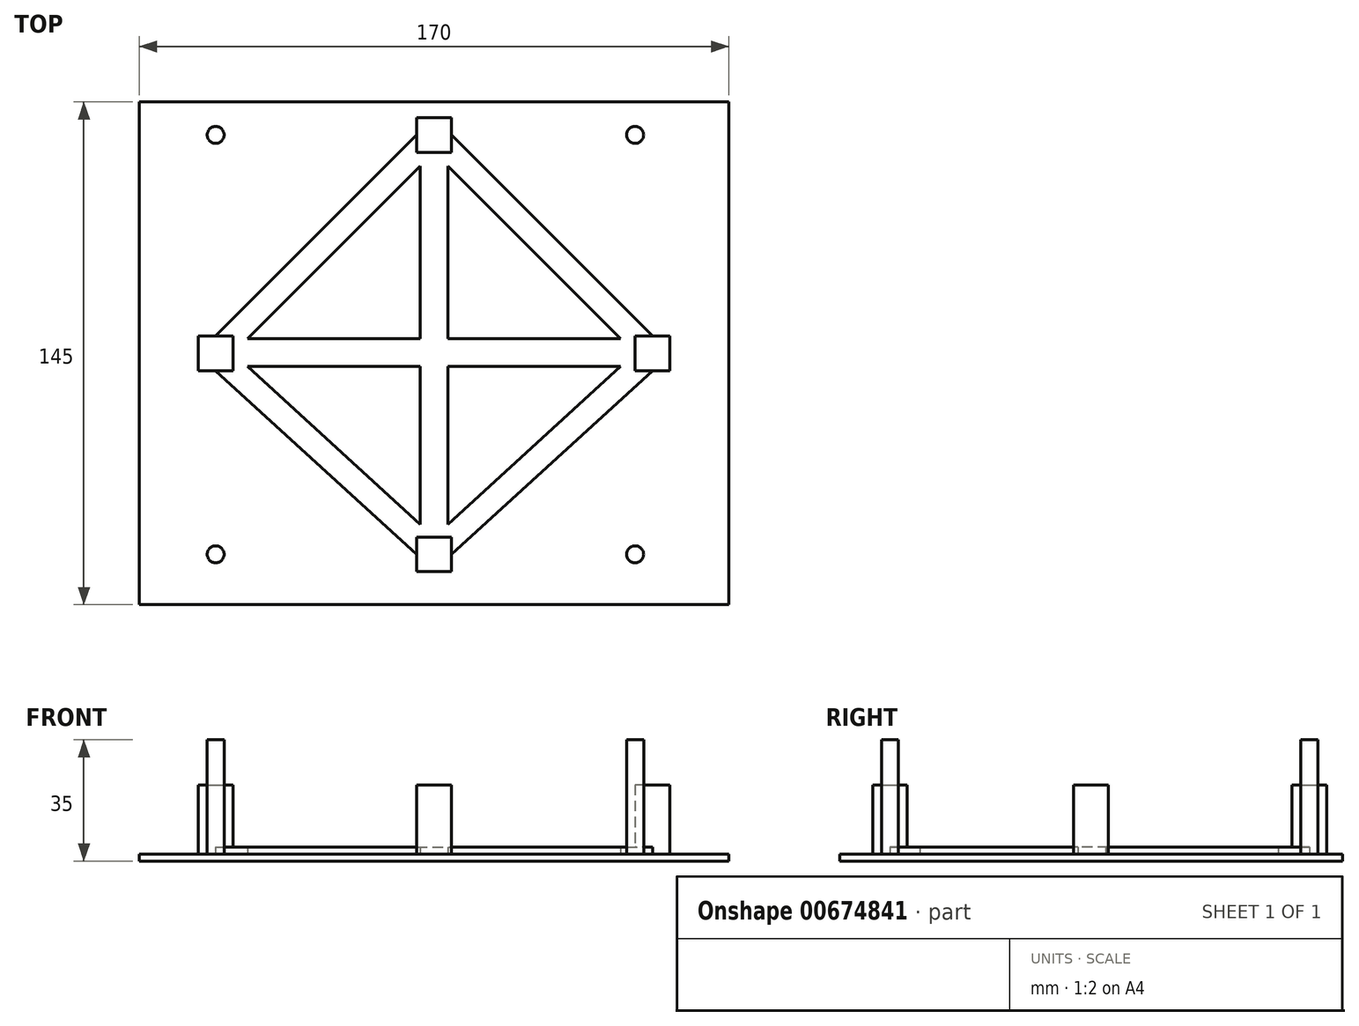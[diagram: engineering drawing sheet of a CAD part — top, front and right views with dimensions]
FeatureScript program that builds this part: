
annotation { "Feature Type Name" : "Feature", "Feature Type Description" : "" }
export const myFeature = defineFeature(function(context is Context, id is Id, definition is map)
    precondition{}
    {
        {
            var Q0;
            Q0=qCreatedBy(makeId("Top.planeOp"),FACE);
            var sketch = newSketch(context, id + "F0", { "sketchPlane" : qUnion([Q0])});
            skLineSegment(sketch, "E0.bottom", {"start": v(0, 0) * mm, "end": v(170, 0) * mm});
            skLineSegment(sketch, "E0.top", {"start": v(0, 145) * mm, "end": v(170, 145) * mm});
            skLineSegment(sketch, "E0.left", {"start": v(0, 0) * mm, "end": v(0, 145) * mm});
            skLineSegment(sketch, "E0.right", {"start": v(170, 0) * mm, "end": v(170, 145) * mm});
            skSolve(sketch);
        }
        {
            var Q0;
            Q0 = qSketchRegion(id + "F0", true);
            extrude(context, id + "F1", {"entities" : qUnion([Q0]), "depth" : 2 * mm, "offsetDistance" : 25 * mm});
        }
        {
            var Q0;
            Q0=makeQuery(id+"F1.opExtrude","CAP_FACE",FACE,{"disambiguationData":[OSD([sQuery(id+"F0.wireOp",EDGE,"E0.bottom"),sQuery(id+"F0.wireOp",EDGE,"E0.top"),sQuery(id+"F0.wireOp",EDGE,"E0.left"),sQuery(id+"F0.wireOp",EDGE,"E0.right")])],"isStart":false});
            var sketch = newSketch(context, id + "F2", { "sketchPlane" : qUnion([Q0])});
            skCircle(sketch, "E1", {"center": v(22, 135.5) * mm, "radius": 2.45 * mm});
            skCircle(sketch, "E2.0.1.0", {"center": v(22, 14.5) * mm, "radius": 2.45 * mm});
            skCircle(sketch, "E2.1.0.0", {"center": v(143, 135.5) * mm, "radius": 2.45 * mm});
            skCircle(sketch, "E2.1.1.0", {"center": v(143, 14.5) * mm, "radius": 2.45 * mm});
            skLineSegment(sketch, "E2.direction1", {"start": v(22, 135.5) * mm, "end": v(143, 135.5) * mm, "construction": true});
            skLineSegment(sketch, "E2.direction2", {"start": v(22, 135.5) * mm, "end": v(22, 14.5) * mm, "construction": true});
            skSolve(sketch);
        }
        {
            var Q0;
            Q0 = qSketchRegion(id + "F2", true);
            extrude(context, id + "F3", {"entities" : qUnion([Q0]), "operationType" : NewBodyOperationType.ADD, "depth" : 33 * mm, "offsetDistance" : 25 * mm});
        }
        {
            var Q0;
            Q0=makeQuery(id+"F1.opExtrude","CAP_FACE",FACE,{"disambiguationData":[OSD([sQuery(id+"F0.wireOp",EDGE,"E0.bottom"),sQuery(id+"F0.wireOp",EDGE,"E0.top"),sQuery(id+"F0.wireOp",EDGE,"E0.left"),sQuery(id+"F0.wireOp",EDGE,"E0.right")])],"isStart":false});
            var sketch = newSketch(context, id + "F4", { "sketchPlane" : qUnion([Q0])});
            skLineSegment(sketch, "E3.bottom", {"start": v(80, 9.5) * mm, "end": v(90, 9.5) * mm});
            skLineSegment(sketch, "E3.top", {"start": v(80, 19.5) * mm, "end": v(90, 19.5) * mm});
            skLineSegment(sketch, "E3.left", {"start": v(80, 9.5) * mm, "end": v(80, 19.5) * mm});
            skLineSegment(sketch, "E3.right", {"start": v(90, 9.5) * mm, "end": v(90, 19.5) * mm});
            skPoint(sketch, "E4", {"position": v(85, 14.5) * mm});
            skLineSegment(sketch, "E5.0.1.0", {"start": v(80, 140.5) * mm, "end": v(90, 140.5) * mm});
            skLineSegment(sketch, "E5.0.1.1", {"start": v(80, 130.5) * mm, "end": v(80, 140.5) * mm});
            skLineSegment(sketch, "E5.0.1.2", {"start": v(80, 130.5) * mm, "end": v(90, 130.5) * mm});
            skLineSegment(sketch, "E5.0.1.3", {"start": v(90, 130.5) * mm, "end": v(90, 140.5) * mm});
            skLineSegment(sketch, "E5.direction1", {"start": v(80, 19.5) * mm, "end": v(105, 19.5) * mm, "construction": true});
            skLineSegment(sketch, "E6.bottom", {"start": v(17, 77.5) * mm, "end": v(27, 77.5) * mm});
            skLineSegment(sketch, "E6.top", {"start": v(17, 67.5) * mm, "end": v(27, 67.5) * mm});
            skLineSegment(sketch, "E6.left", {"start": v(17, 77.5) * mm, "end": v(17, 67.5) * mm});
            skLineSegment(sketch, "E6.right", {"start": v(27, 77.5) * mm, "end": v(27, 67.5) * mm});
            skLineSegment(sketch, "E7.MirrorCS", {"start": v(153, 77.5) * mm, "end": v(143, 77.5) * mm});
            skLineSegment(sketch, "E8.MirrorCS", {"start": v(143, 77.5) * mm, "end": v(143, 67.5) * mm});
            skLineSegment(sketch, "E9.MirrorCS", {"start": v(153, 77.5) * mm, "end": v(153, 67.5) * mm});
            skLineSegment(sketch, "E10.MirrorCS", {"start": v(153, 67.5) * mm, "end": v(143, 67.5) * mm});
            skSolve(sketch);
        }
        {
            var Q0;
            Q0 = qSketchRegion(id + "F4", true);
            extrude(context, id + "F5", {"entities" : qUnion([Q0]), "operationType" : NewBodyOperationType.ADD, "depth" : 20 * mm, "offsetDistance" : 25 * mm});
        }
        {
            var Q0;
            Q0=makeQuery(id+"F5.opExtrude","SWEPT_FACE",FACE,{"disambiguationData":[OSD([sQuery(id+"F4.wireOp",EDGE,"E8.MirrorCS")])]});
            var sketch = newSketch(context, id + "F6", { "sketchPlane" : qUnion([Q0])});
            skLineSegment(sketch, "E11.0", {"start": v(-77.5, 22) * mm, "end": v(-77.5, 2) * mm});
            skLineSegment(sketch, "E12.0", {"start": v(-67.5, 22) * mm, "end": v(-67.5, 2) * mm});
            skPoint(sketch, "E13.0", {"position": v(-72.5, 2) * mm});
            skLineSegment(sketch, "E14.0", {"start": v(-77.5, 2) * mm, "end": v(-67.5, 2) * mm});
            skLineSegment(sketch, "E15", {"start": v(-77.5, 9.96) * mm, "end": v(-67.5, 9.96) * mm});
            skSolve(sketch);
        }
        {
            var Q0;
            Q0=makeQuery(id+"F1.opExtrude","CAP_FACE",FACE,{"disambiguationData":[OSD([sQuery(id+"F0.wireOp",EDGE,"E0.bottom"),sQuery(id+"F0.wireOp",EDGE,"E0.top"),sQuery(id+"F0.wireOp",EDGE,"E0.left"),sQuery(id+"F0.wireOp",EDGE,"E0.right")])],"isStart":false});
            var sketch = newSketch(context, id + "F7", { "sketchPlane" : qUnion([Q0])});
            skPoint(sketch, "E16.0", {"position": v(22, 77.5) * mm});
            skLineSegment(sketch, "E17.0", {"start": v(27, 72.5) * mm, "end": v(27, 67.5) * mm});
            skPoint(sketch, "E18.0", {"position": v(85, 19.5) * mm});
            skLineSegment(sketch, "E19.0", {"start": v(80, 19.5) * mm, "end": v(90, 19.5) * mm});
            skLineSegment(sketch, "E20.0", {"start": v(90, 14.5) * mm, "end": v(90, 19.5) * mm});
            skLineSegment(sketch, "E21.0", {"start": v(80, 14.5) * mm, "end": v(80, 19.5) * mm});
            skLineSegment(sketch, "E22.0", {"start": v(143, 77.5) * mm, "end": v(143, 67.5) * mm});
            skLineSegment(sketch, "E23.0", {"start": v(148, 77.5) * mm, "end": v(143, 77.5) * mm});
            skPoint(sketch, "E24.0", {"position": v(153, 72.5) * mm});
            skLineSegment(sketch, "E25.0", {"start": v(148, 67.5) * mm, "end": v(143, 67.5) * mm});
            skLineSegment(sketch, "E26.0", {"start": v(80, 130.5) * mm, "end": v(90, 130.5) * mm});
            skPoint(sketch, "E27.0", {"position": v(80, 135.5) * mm});
            skLineSegment(sketch, "E28.0", {"start": v(80, 130.5) * mm, "end": v(80, 135.5) * mm});
            skLineSegment(sketch, "E29.0", {"start": v(90, 130.5) * mm, "end": v(90, 135.5) * mm});
            skLineSegment(sketch, "E30", {"start": v(22, 77.5) * mm, "end": v(80, 135.5) * mm});
            skLineSegment(sketch, "E31", {"start": v(27, 72.5) * mm, "end": v(85, 130.5) * mm});
            skLineSegment(sketch, "E32", {"start": v(143, 72.5) * mm, "end": v(85, 130.5) * mm});
            skLineSegment(sketch, "E33", {"start": v(90, 135.5) * mm, "end": v(148, 77.5) * mm});
            skLineSegment(sketch, "E34", {"start": v(85, 19.5) * mm, "end": v(143, 72.5) * mm});
            skLineSegment(sketch, "E35", {"start": v(90, 14.5) * mm, "end": v(148, 67.5) * mm});
            skLineSegment(sketch, "E36", {"start": v(27, 72.5) * mm, "end": v(85, 19.5) * mm});
            skLineSegment(sketch, "E37", {"start": v(22, 67.5) * mm, "end": v(80, 14.5) * mm});
            skPoint(sketch, "E38.orphan", {"position": v(27, 77.5) * mm});
            skPoint(sketch, "E39.0.start.orphan", {"position": v(17, 77.5) * mm});
            skPoint(sketch, "E40.orphan", {"position": v(17, 67.5) * mm});
            skLineSegment(sketch, "E41", {"start": v(27, 72.5) * mm, "end": v(27, 77.5) * mm});
            skLineSegment(sketch, "E42", {"start": v(22, 67.5) * mm, "end": v(27, 67.5) * mm});
            skLineSegment(sketch, "E43", {"start": v(22, 77.5) * mm, "end": v(27, 77.5) * mm});
            skPoint(sketch, "E44.0.start.orphan", {"position": v(80, 9.5) * mm});
            skPoint(sketch, "E45.orphan", {"position": v(90, 9.5) * mm});
            skPoint(sketch, "E46.orphan", {"position": v(153, 77.5) * mm});
            skPoint(sketch, "E47.orphan", {"position": v(153, 67.5) * mm});
            skPoint(sketch, "E48.orphan", {"position": v(80, 140.5) * mm});
            skPoint(sketch, "E49.orphan", {"position": v(90, 140.5) * mm});
            skSolve(sketch);
        }
        {
            var Q0;
            Q0=makeQuery(id+"F7.imprint","IMPRINT",FACE,{"disambiguationData":[TD([[makeQuery(id+"F7.imprint","IMPRINT",EDGE,{"derivedFrom":sQuery(id+"F7.wireOp",EDGE,"E17.0")}),1.0]])]});
            var Q1;
            {var subQ3=sQuery(id+"F7.wireOp",EDGE,"E20.0");Q1=makeQuery(id+"F7.imprint","IMPRINT",FACE,{"disambiguationData":[TD([[makeQuery(id+"F7.imprint","IMPRINT",EDGE,{"derivedFrom":subQ3}),-1.0]])]});}
            var Q2;
            {var subQ1=sQuery(id+"F7.wireOp",EDGE,"E23.0");Q2=makeQuery(id+"F7.imprint","IMPRINT",FACE,{"disambiguationData":[TD([[makeQuery(id+"F7.imprint","IMPRINT",EDGE,{"derivedFrom":subQ1}),-1.0]])]});}
            var Q3;
            {var subQ0=sQuery(id+"F7.wireOp",EDGE,"E28.0");Q3=makeQuery(id+"F7.imprint","IMPRINT",FACE,{"disambiguationData":[TD([[makeQuery(id+"F7.imprint","IMPRINT",EDGE,{"derivedFrom":subQ0}),1.0]])]});}
            extrude(context, id + "F8", {"entities" : qUnion([Q0, Q1, Q2, Q3]), "operationType" : NewBodyOperationType.ADD, "depth" : 2 * mm, "offsetDistance" : 25 * mm});
        }
        {
            var Q0;
            Q0=makeQuery(id+"F8.boolean.opBoolean","SPLIT",FACE,{"disambiguationData":[TD([makeQuery(id+"F8.opExtrude","SWEPT_FACE",FACE,{"disambiguationData":[OSD([sQuery(id+"F7.wireOp",EDGE,"E31")])]})])],"derivedFrom":makeQuery(id+"F1.opExtrude","CAP_FACE",FACE,{"disambiguationData":[OSD([sQuery(id+"F0.wireOp",EDGE,"E0.bottom"),sQuery(id+"F0.wireOp",EDGE,"E0.top"),sQuery(id+"F0.wireOp",EDGE,"E0.left"),sQuery(id+"F0.wireOp",EDGE,"E0.right")])],"isStart":false})});
            var sketch = newSketch(context, id + "F9", { "sketchPlane" : qUnion([Q0])});
            skLineSegment(sketch, "E50", {"start": v(81, 23.16) * mm, "end": v(81, 126.5) * mm});
            skLineSegment(sketch, "E51", {"start": v(81, 126.5) * mm, "end": v(85, 130.5) * mm});
            skLineSegment(sketch, "E52", {"start": v(85, 130.5) * mm, "end": v(89, 126.5) * mm});
            skLineSegment(sketch, "E53", {"start": v(89, 126.5) * mm, "end": v(89, 23.16) * mm});
            skLineSegment(sketch, "E54", {"start": v(89, 23.16) * mm, "end": v(85, 19.5) * mm});
            skLineSegment(sketch, "E55", {"start": v(85, 19.5) * mm, "end": v(81, 23.16) * mm});
            skLineSegment(sketch, "E56", {"start": v(31.18, 68.68) * mm, "end": v(27, 72.5) * mm});
            skLineSegment(sketch, "E57", {"start": v(27, 72.5) * mm, "end": v(31.18, 76.68) * mm});
            skLineSegment(sketch, "E58", {"start": v(31.18, 76.68) * mm, "end": v(138.82, 76.68) * mm});
            skLineSegment(sketch, "E59", {"start": v(138.82, 76.68) * mm, "end": v(143, 72.5) * mm});
            skLineSegment(sketch, "E60", {"start": v(143, 72.5) * mm, "end": v(139.18, 68.68) * mm});
            skLineSegment(sketch, "E61", {"start": v(139.18, 68.68) * mm, "end": v(31.18, 68.68) * mm});
            skSolve(sketch);
        }
        {
            var Q0;
            {var subQ6=sQuery(id+"F9.wireOp",EDGE,"E56");Q0=makeQuery(id+"F9.imprint","IMPRINT",FACE,{"disambiguationData":[TD([[makeQuery(id+"F9.imprint","IMPRINT",EDGE,{"derivedFrom":subQ6}),1.0]])]});}
            var Q1;
            {var subQ4=sQuery(id+"F9.wireOp",EDGE,"E51");Q1=makeQuery(id+"F9.imprint","IMPRINT",FACE,{"disambiguationData":[TD([[makeQuery(id+"F9.imprint","IMPRINT",EDGE,{"derivedFrom":subQ4}),-1.0]])]});}
            var Q2;
            {var subQ0=sQuery(id+"F9.wireOp",EDGE,"E61");var subQ1=sQuery(id+"F9.wireOp",EDGE,"E50");var subQ2=makeQuery(id+"F9.imprint","INTERSECT",VERTEX,{"derivedFrom":[subQ1,subQ0]});Q2=makeQuery(id+"F9.imprint","IMPRINT",FACE,{"disambiguationData":[TD([[makeQuery(id+"F9.imprint","IMPRINT",EDGE,{"disambiguationData":[TD([[subQ2,-1.0]])],"derivedFrom":subQ1}),-1.0]])]});}
            var Q3;
            {var subQ0=sQuery(id+"F9.wireOp",EDGE,"E60");Q3=makeQuery(id+"F9.imprint","IMPRINT",FACE,{"disambiguationData":[TD([[makeQuery(id+"F9.imprint","IMPRINT",EDGE,{"derivedFrom":subQ0}),-1.0]])]});}
            var Q4;
            {var subQ5=sQuery(id+"F9.wireOp",EDGE,"E59");Q4=makeQuery(id+"F9.imprint","IMPRINT",FACE,{"disambiguationData":[TD([[makeQuery(id+"F9.imprint","IMPRINT",EDGE,{"derivedFrom":subQ5}),1.0]])]});}
            var Q5;
            {var subQ1=sQuery(id+"F9.wireOp",EDGE,"E54");Q5=makeQuery(id+"F9.imprint","IMPRINT",FACE,{"disambiguationData":[TD([[makeQuery(id+"F9.imprint","IMPRINT",EDGE,{"derivedFrom":subQ1}),1.0]])]});}
            extrude(context, id + "F10", {"entities" : qUnion([Q0, Q1, Q2, Q3, Q4, Q5]), "operationType" : NewBodyOperationType.ADD, "depth" : 2 * mm, "offsetDistance" : 25 * mm});
        }
    });
